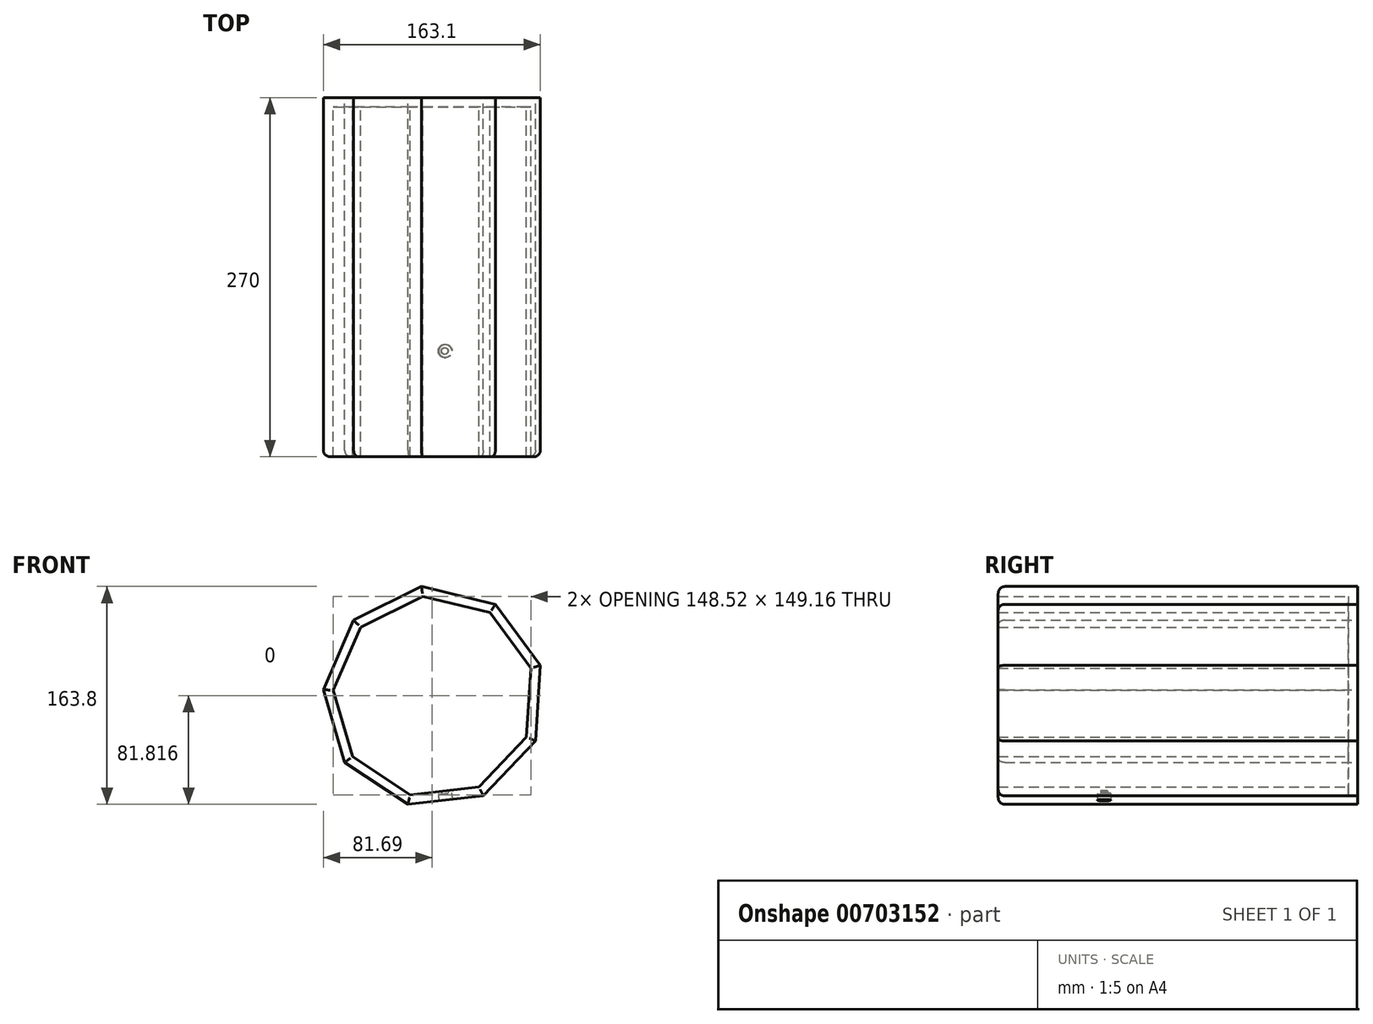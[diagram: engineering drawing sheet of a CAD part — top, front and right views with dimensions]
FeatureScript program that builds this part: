
annotation { "Feature Type Name" : "Feature", "Feature Type Description" : "" }
export const myFeature = defineFeature(function(context is Context, id is Id, definition is map)
    precondition{}
    {
        {
            var Q0;
            Q0=qCreatedBy(makeId("Front.planeOp"),FACE);
            var sketch = newSketch(context, id + "F0", { "sketchPlane" : qUnion([Q0])});
            skCircle(sketch, "E0.cCircle", {"center": v(0, 0) * mm, "radius": 83.33 * mm, "construction": true});
            skLineSegment(sketch, "E0.0", {"start": v(76.36, -33.35) * mm, "end": v(37.06, -74.63) * mm});
            skLineSegment(sketch, "E0.1", {"start": v(37.06, -74.63) * mm, "end": v(-19.58, -81) * mm});
            skLineSegment(sketch, "E0.2", {"start": v(-19.58, -81) * mm, "end": v(-67.06, -49.46) * mm});
            skLineSegment(sketch, "E0.3", {"start": v(-67.06, -49.46) * mm, "end": v(-83.16, 5.22) * mm});
            skLineSegment(sketch, "E0.4", {"start": v(-83.16, 5.22) * mm, "end": v(-60.35, 57.46) * mm});
            skLineSegment(sketch, "E0.5", {"start": v(-60.35, 57.46) * mm, "end": v(-9.3, 82.8) * mm});
            skLineSegment(sketch, "E0.6", {"start": v(-9.3, 82.8) * mm, "end": v(46.1, 69.41) * mm});
            skLineSegment(sketch, "E0.7", {"start": v(46.1, 69.41) * mm, "end": v(79.94, 23.54) * mm});
            skLineSegment(sketch, "E0.8", {"start": v(79.94, 23.54) * mm, "end": v(76.36, -33.35) * mm});
            skSolve(sketch);
        }
        {
            var Q0;
            Q0 = qSketchRegion(id + "F0", true);
            extrude(context, id + "F1", {"entities" : qUnion([Q0]), "depth" : 270 * mm, "offsetDistance" : 25 * mm});
        }
        {
            var Q0;
            Q0=makeQuery(id+"F1.opExtrude","CAP_FACE",FACE,{"disambiguationData":[OSD([sQuery(id+"F0.wireOp",EDGE,"E0.0"),sQuery(id+"F0.wireOp",EDGE,"E0.1"),sQuery(id+"F0.wireOp",EDGE,"E0.2"),sQuery(id+"F0.wireOp",EDGE,"E0.3"),sQuery(id+"F0.wireOp",EDGE,"E0.4"),sQuery(id+"F0.wireOp",EDGE,"E0.5"),sQuery(id+"F0.wireOp",EDGE,"E0.6"),sQuery(id+"F0.wireOp",EDGE,"E0.7"),sQuery(id+"F0.wireOp",EDGE,"E0.8")])],"isStart":false});
            shell(context, id + "F2", {"entities" : qUnion([Q0]), "thickness" : 7 * mm});
        }
        {
            var Q0;
            Q0=makeQuery(id+"F1.opExtrude","SWEPT_FACE",FACE,{"disambiguationData":[OSD([sQuery(id+"F0.wireOp",EDGE,"E0.1")])]});
            var sketch = newSketch(context, id + "F3", { "sketchPlane" : qUnion([Q0])});
            skCircle(sketch, "E1", {"center": v(0, 190.98) * mm, "radius": 19.16 * mm});
            skSolve(sketch);
        }
        {
            var Q0;
            Q0=makeQuery(id+"F3.imprint","IMPRINT",FACE,{"disambiguationData":[TD([[makeQuery(id+"F3.imprint","IMPRINT",EDGE,{"derivedFrom":sQuery(id+"F3.wireOp",EDGE,"E1")}),1.0]])]});
            var sketch = newSketch(context, id + "F4", { "sketchPlane" : qUnion([Q0])});
            skPoint(sketch, "E2", {"position": v(0, 190.45) * mm});
            skSolve(sketch);
        }
        {
            var Q0;
            Q0=sQuery(id+"F4.wireOp",VERTEX,"E2");
            var Q1;
            Q1=makeQuery(id+"F1.opExtrude","SWEPT_BODY",BODY,{"disambiguationData":[OSD([sQuery(id+"F0.wireOp",EDGE,"E0.0"),sQuery(id+"F0.wireOp",EDGE,"E0.1"),sQuery(id+"F0.wireOp",EDGE,"E0.2"),sQuery(id+"F0.wireOp",EDGE,"E0.3"),sQuery(id+"F0.wireOp",EDGE,"E0.4"),sQuery(id+"F0.wireOp",EDGE,"E0.5"),sQuery(id+"F0.wireOp",EDGE,"E0.6"),sQuery(id+"F0.wireOp",EDGE,"E0.7"),sQuery(id+"F0.wireOp",EDGE,"E0.8")])]});
            hole(context, id + "F5", {"style" : HoleStyle.C_BORE, "endStyle" : HoleEndStyle.BLIND, "holeDiameter" : 5 * mm, "cBoreDiameter" : 10 * mm, "cBoreDepth" : 5 * mm, "majorDiameter" : 5 * mm, "holeDepth" : 20 * mm, "isTappedThrough" : true, "tappedDepth" : 12 * mm, "tapClearance" : 3, "locations" : qUnion([Q0]), "scope" : qUnion([Q1])});
        }
        {
            var Q0;
            Q0=makeQuery(id+"F1.opExtrude","CAP_EDGE",EDGE,{"disambiguationData":[OSD([sQuery(id+"F0.wireOp",EDGE,"E0.3")])],"isStart":false});
            var Q1;
            Q1=makeQuery(id+"F1.opExtrude","CAP_EDGE",EDGE,{"disambiguationData":[OSD([sQuery(id+"F0.wireOp",EDGE,"E0.1")])],"isStart":false});
            var Q2;
            Q2=makeQuery(id+"F1.opExtrude","CAP_EDGE",EDGE,{"disambiguationData":[OSD([sQuery(id+"F0.wireOp",EDGE,"E0.0")])],"isStart":false});
            var Q3;
            Q3=makeQuery(id+"F1.opExtrude","CAP_EDGE",EDGE,{"disambiguationData":[OSD([sQuery(id+"F0.wireOp",EDGE,"E0.2")])],"isStart":false});
            var Q4;
            Q4=makeQuery(id+"F1.opExtrude","CAP_EDGE",EDGE,{"disambiguationData":[OSD([sQuery(id+"F0.wireOp",EDGE,"E0.8")])],"isStart":false});
            var Q5;
            Q5=makeQuery(id+"F1.opExtrude","CAP_EDGE",EDGE,{"disambiguationData":[OSD([sQuery(id+"F0.wireOp",EDGE,"E0.7")])],"isStart":false});
            var Q6;
            Q6=makeQuery(id+"F1.opExtrude","CAP_EDGE",EDGE,{"disambiguationData":[OSD([sQuery(id+"F0.wireOp",EDGE,"E0.6")])],"isStart":false});
            var Q7;
            Q7=makeQuery(id+"F1.opExtrude","CAP_EDGE",EDGE,{"disambiguationData":[OSD([sQuery(id+"F0.wireOp",EDGE,"E0.5")])],"isStart":false});
            var Q8;
            Q8=makeQuery(id+"F1.opExtrude","CAP_EDGE",EDGE,{"disambiguationData":[OSD([sQuery(id+"F0.wireOp",EDGE,"E0.4")])],"isStart":false});
            fillet(context, id + "F6", {"entities" : qUnion([Q0, Q1, Q2, Q3, Q4, Q5, Q6, Q7, Q8]), "radius" : 5 * mm, "tangentPropagation" : true, "allowEdgeOverflow" : false});
        }
    });
